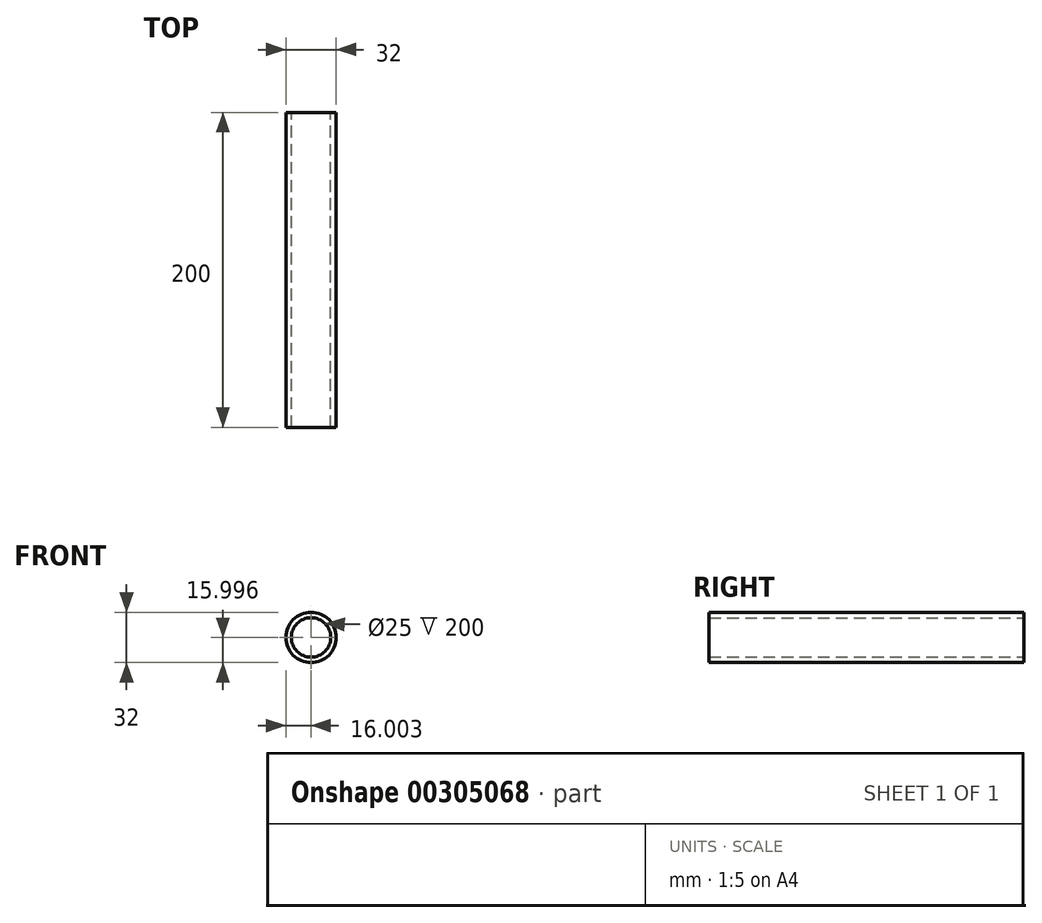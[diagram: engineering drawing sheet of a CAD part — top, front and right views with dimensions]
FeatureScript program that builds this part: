
annotation { "Feature Type Name" : "Feature", "Feature Type Description" : "" }
export const myFeature = defineFeature(function(context is Context, id is Id, definition is map)
    precondition{}
    {
        {
            var Q0;
            Q0=qCreatedBy(makeId("Front.planeOp"),FACE);
            var sketch = newSketch(context, id + "F0", { "sketchPlane" : qUnion([Q0])});
            skCircle(sketch, "E0", {"center": v(-51.57, 33.57) * mm, "radius": 12.5 * mm});
            skCircle(sketch, "E1.0", {"center": v(-51.57, 33.57) * mm, "radius": 16 * mm});
            skSolve(sketch);
        }
        {
            var Q0;
            Q0=qSketchRegion(id+"F0",true);
            extrude(context, id + "F1", {"entities" : qUnion([Q0]), "flatOperationType" : FlatOperationType.REMOVE, "offsetDistance" : 25 * mm, "depth" : 200 * mm, "domain" : OperationDomain.MODEL});
        }
    });
